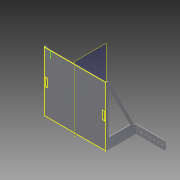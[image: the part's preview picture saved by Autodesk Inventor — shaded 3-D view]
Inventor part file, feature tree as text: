
AUTODESK INVENTOR PART (.ipt)
format: ipt  version: 2014 SP1 (Build 180222100, 222)  size: 365,056 bytes
history: native  units: in
note: dims shown in document units (in); Inventor stores cm internally (conversion verified against a paired STEP export)
features: sketch x12, other x12, sheet_metal_op x10, chamfer x3, pattern_linear x1, plane x1, mirror x1
ambient origin geometry x8: Origin, YZ Plane, XZ Plane, XY Plane, X Axis, Y Axis, Z Axis, Center Point
bodies: Solid1 (feature_tree)
feature tree (40):
  sheet_metal_op  "Face1"
  sheet_metal_op  "Flange1"
  sheet_metal_op  "Flange2"
  sheet_metal_op  "Flange3"
  chamfer  "Corner Round1"
  chamfer  "Corner Round2"
  chamfer  "Corner Round3"
  sketch  "Sketch12"  dims[d10=0.0625in]
  pattern_linear  "Rectangular Pattern2"  Spacing1=0.125in  [1 undecoded]
  plane  "Work Plane1"
  mirror  "Mirror1"
  sketch  "Sketch1"  dims[d0=7.1in]
  other  "Plate1"
  sketch  "Sketch2"  dims[d1=7.35in]
  other  "Plate2"
  sheet_metal_op  "Bend1"
  sheet_metal_op  "Corner1"
  sketch  "Sketch3"  dims[d2=0.125in]
  other  "Plate3"
  sheet_metal_op  "Bend2"
  sheet_metal_op  "Corner2"
  sketch  "Sketch4"  dims[d3=0.5in]
  other  "Plate4"
  sheet_metal_op  "Bend3"
  sheet_metal_op  "Corner3"
  sketch  "Sketch5"  dims[d4=0.25in]
  sketch  "Sketch6"  dims[d5=1.0in]
  sketch  "Sketch7"  dims[d6=0.125in]
  sketch  "Sketch8"  dims[d7=0.25in]
  sketch  "Sketch9"  dims[d8=1.0in]
  sketch  "Sketch10"  dims[d9=0.0625in]
  sketch  "Sketch14"  dims[d11=0.0312in d12=0.125in d13=0.0625in d14=3.5in d15=90.0deg d16=0.005in d17=0.25in d18=0.0625in d19=0.0625in d20=0.0625in d21=0.0312in d22=0.125in d23=0.0625in d24=3.5in d25=90.0deg d26=0.005in d27=0.25in d28=0.0625in d29=0.0625in d30=0.0625in d31=0.0312in d32=0.125in d33=0.0625in d34=3.5in d35=90.0deg d36=0.005in d37=0.25in d38=0.0625in d39=0.0625in d40=3.5625in d41=6.1in d42=0.25in d43=0.0in d44=3.563in d45=6.1in d46=0.25in d47=0.0in d48=0.25in d49=0.0625in d50=0.0in d51=0.25in d52=0.0625in d53=0.0in d54=0.125in d55=0.125in d56=0.25in d57=0.25in d58=0.25in d59=0.0625in d60=0.0in d61=0.0625in d62=0.0in d63=0.125in d66=0.375in d67=0.191in d68=0.0625in d69=0.0in d73=2.3622in d75=0.5in d76=3.66in]
  other  "Cut1"
  other  "Cut2"
  other  "Cut3"
  other  "Cut4"
  other  "Cut5"
  other  "Cut6"
  other  "Cut8"
  other  "Definition1"
note: 1 required parameter value undecoded (feature->parameter linkage not recoverable at this tier; creation-order binding heuristic only, values carry confidence <= 0.55)
